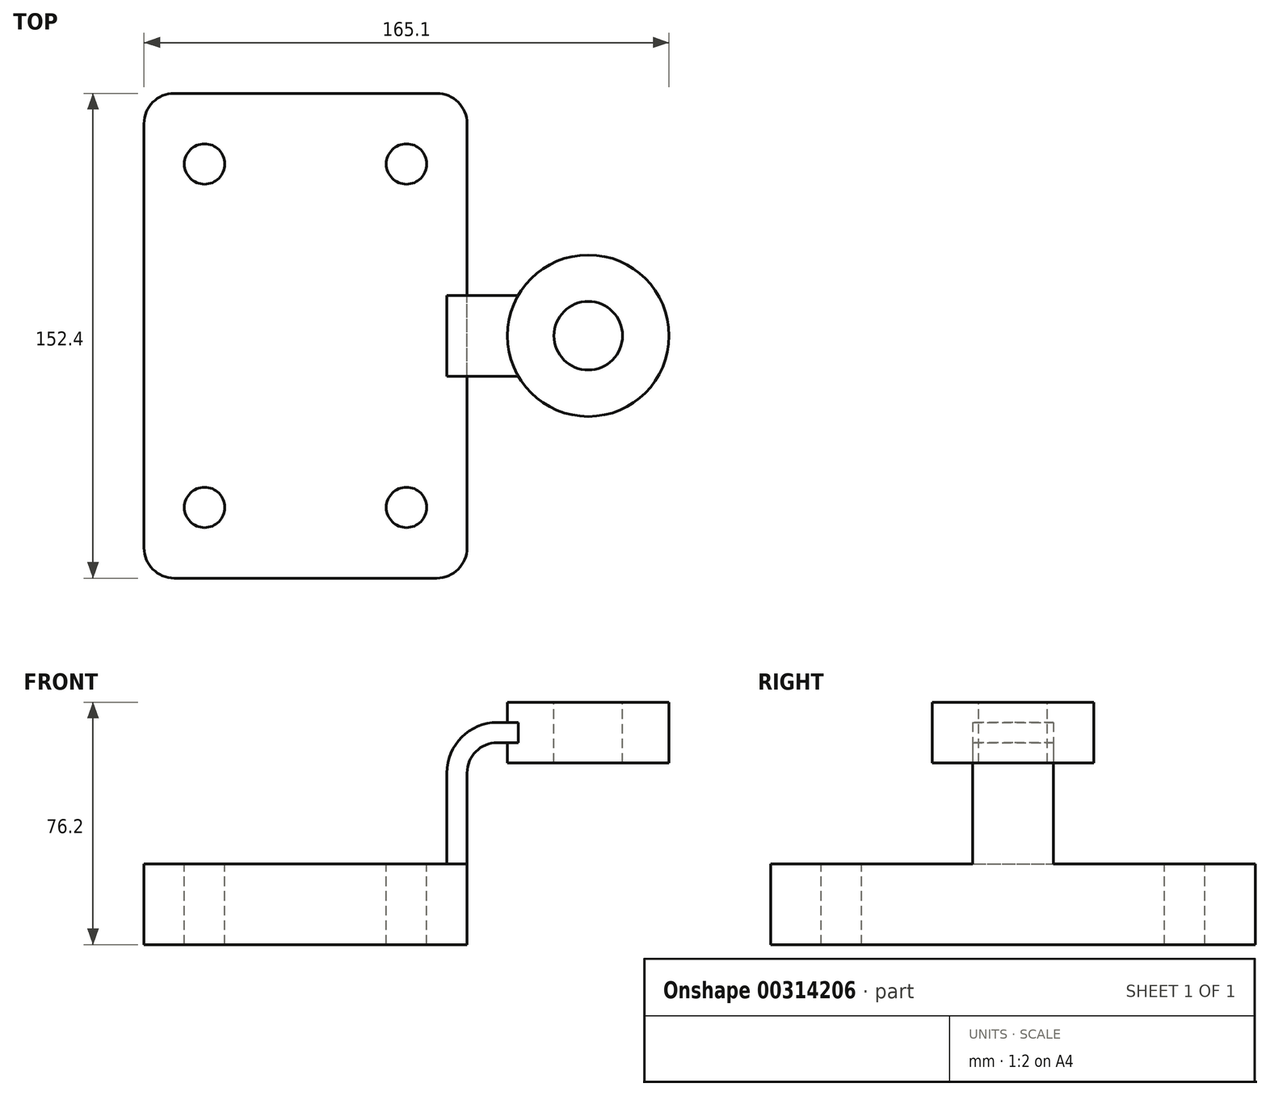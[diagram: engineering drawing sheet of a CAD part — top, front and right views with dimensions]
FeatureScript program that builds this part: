
annotation { "Feature Type Name" : "Feature", "Feature Type Description" : "" }
export const myFeature = defineFeature(function(context is Context, id is Id, definition is map)
    precondition{}
    {
        {
            var Q0;
            Q0=qCreatedBy(makeId("Front.planeOp"),FACE);
            var sketch = newSketch(context, id + "F0", { "sketchPlane" : qUnion([Q0])});
            skLineSegment(sketch, "E0.bottom", {"start": v(-50.8, -12.7) * mm, "end": v(50.8, -12.7) * mm});
            skLineSegment(sketch, "E0.top", {"start": v(-50.8, 12.7) * mm, "end": v(50.8, 12.7) * mm});
            skLineSegment(sketch, "E0.left", {"start": v(-50.8, -12.7) * mm, "end": v(-50.8, 12.7) * mm});
            skLineSegment(sketch, "E0.right", {"start": v(50.8, -12.7) * mm, "end": v(50.8, 12.7) * mm});
            skPoint(sketch, "E0.middle", {"position": v(0, 0) * mm});
            skLineSegment(sketch, "E1.bottom", {"start": v(88.9, 44.45) * mm, "end": v(114.3, 44.45) * mm});
            skLineSegment(sketch, "E1.top", {"start": v(88.9, 63.5) * mm, "end": v(114.3, 63.5) * mm});
            skLineSegment(sketch, "E1.left", {"start": v(88.9, 44.45) * mm, "end": v(88.9, 63.5) * mm});
            skLineSegment(sketch, "E1.right", {"start": v(114.3, 44.45) * mm, "end": v(114.3, 63.5) * mm});
            skPoint(sketch, "E1.middle", {"position": v(101.6, 53.98) * mm});
            skPoint(sketch, "E2.middle", {"position": v(88.9, 63.5) * mm});
            skLineSegment(sketch, "E3", {"start": v(50.8, 12.7) * mm, "end": v(50.8, 41.28) * mm});
            skArc(sketch, "E4", {"start": v(50.8, 41.28) * mm, "mid": v(53.59, 48.01) * mm, "end": v(60.32, 50.8) * mm});
            skLineSegment(sketch, "E5", {"start": v(60.32, 50.8) * mm, "end": v(88.9, 50.8) * mm});
            skLineSegment(sketch, "E6.0", {"start": v(60.32, 57.15) * mm, "end": v(88.9, 57.15) * mm});
            skArc(sketch, "E6.1", {"start": v(44.45, 41.28) * mm, "mid": v(49.1, 52.5) * mm, "end": v(60.32, 57.15) * mm});
            skLineSegment(sketch, "E6.2", {"start": v(44.45, 12.7) * mm, "end": v(44.45, 41.28) * mm});
            skFitSpline(sketch, "E7", {"points": [v(-50.8, 12.7) * mm, v(-2.37, 52.03) * mm, v(60.32, 57.15) * mm], "startDerivative": vector(86.36, 73.43) * mm, "endDerivative": vector(124.87, 0) * mm});
            skLineSegment(sketch, "E8", {"start": v(88.9, 57.15) * mm, "end": v(88.9, 50.8) * mm});
            skSolve(sketch);
        }
        {
            var Q0;
            Q0=makeQuery(id+"F0.imprint","IMPRINT",FACE,{"disambiguationData":[TD([[makeQuery(id+"F0.imprint","IMPRINT",EDGE,{"derivedFrom":sQuery(id+"F0.wireOp",EDGE,"E0.bottom")}),1.0]])]});
            extrude(context, id + "F1", {"entities" : qUnion([Q0]), "endBound" : BoundingType.SYMMETRIC, "depth" : 152.4 * mm});
        }
        {
            var Q0;
            {var subQ0=sQuery(id+"F0.wireOp",EDGE,"E3");Q0=makeQuery(id+"F0.imprint","IMPRINT",FACE,{"disambiguationData":[TD([[makeQuery(id+"F0.imprint","IMPRINT",EDGE,{"derivedFrom":subQ0}),1.0]])]});}
            extrude(context, id + "F2", {"entities" : qUnion([Q0]), "operationType" : NewBodyOperationType.ADD, "endBound" : BoundingType.SYMMETRIC, "depth" : 25.4 * mm});
        }
        {
            var Q0;
            Q0=makeQuery(id+"F0.imprint","IMPRINT",FACE,{"disambiguationData":[TD([[makeQuery(id+"F0.imprint","IMPRINT",EDGE,{"derivedFrom":sQuery(id+"F0.wireOp",EDGE,"E6.1")}),1.0]])]});
            extrude(context, id + "F3", {"entities" : qUnion([Q0]), "operationType" : NewBodyOperationType.ADD, "endBound" : BoundingType.SYMMETRIC, "depth" : 12.7 * mm});
        }
        {
            var Q0;
            {var subQ3=sQuery(id+"F0.wireOp",EDGE,"E1.bottom");Q0=makeQuery(id+"F0.imprint","IMPRINT",FACE,{"disambiguationData":[TD([[makeQuery(id+"F0.imprint","IMPRINT",EDGE,{"derivedFrom":subQ3}),1.0]])]});}
            var Q1;
            Q1=sQuery(id+"F0.wireOp",EDGE,"E1.left");
            revolve(context, id + "F4", {"operationType" : NewBodyOperationType.ADD, "entities" : qUnion([Q0]), "axis" : qUnion([Q1]), "revolveType" : RevolveType.FULL});
        }
        {
            var Q0;
            Q0=makeQuery(id+"F1.opExtrude","CAP_EDGE",EDGE,{"disambiguationData":[OSD([sQuery(id+"F0.wireOp",EDGE,"E0.right")])],"isStart":false});
            var Q1;
            Q1=makeQuery(id+"F1.opExtrude","CAP_EDGE",EDGE,{"disambiguationData":[OSD([sQuery(id+"F0.wireOp",EDGE,"E0.right")])],"isStart":true});
            var Q2;
            Q2=makeQuery(id+"F1.opExtrude","CAP_EDGE",EDGE,{"disambiguationData":[OSD([sQuery(id+"F0.wireOp",EDGE,"E0.left")])],"isStart":true});
            var Q3;
            Q3=makeQuery(id+"F1.opExtrude","CAP_EDGE",EDGE,{"disambiguationData":[OSD([sQuery(id+"F0.wireOp",EDGE,"E0.left")])],"isStart":false});
            fillet(context, id + "F5", {"entities" : qUnion([Q0, Q1, Q2, Q3]), "radius" : 9.52 * mm, "tangentPropagation" : true, "allowEdgeOverflow" : false});
        }
        {
            var Q0;
            Q0=makeQuery(id+"F4.opRevolve","SWEPT_FACE",FACE,{"disambiguationData":[OSD([sQuery(id+"F0.wireOp",EDGE,"E1.top")])]});
            var sketch = newSketch(context, id + "F6", { "sketchPlane" : qUnion([Q0])});
            skCircle(sketch, "E9", {"center": v(88.9, 0) * mm, "radius": 10.78 * mm});
            skSolve(sketch);
        }
        {
            var Q0;
            Q0=makeQuery(id+"F6.imprint","IMPRINT",FACE,{"disambiguationData":[TD([[makeQuery(id+"F6.imprint","IMPRINT",EDGE,{"derivedFrom":sQuery(id+"F6.wireOp",EDGE,"E9")}),1.0]])]});
            var Q1;
            Q1=sQuery(id+"F6.wireOp",EDGE,"E9");
            var Q2;
            Q2=makeQuery(id+"F4.opRevolve","SWEPT_FACE",FACE,{"disambiguationData":[OSD([sQuery(id+"F0.wireOp",EDGE,"E1.bottom")])]});
            var Q3;
            Q3=makeQuery(id+"F4.opRevolve","SWEPT_FACE",FACE,{"disambiguationData":[OSD([sQuery(id+"F0.wireOp",EDGE,"E1.bottom")])]});
            extrude(context, id + "F7", {"entities" : qUnion([Q0]), "operationType" : NewBodyOperationType.REMOVE, "surfaceEntities" : qUnion([Q1]), "endBound" : BoundingType.THROUGH_ALL, "oppositeDirection" : true, "endBoundEntityFace" : qUnion([Q2]), "depth" : 25.4 * mm});
        }
        {
            var Q0;
            Q0=qCreatedBy(makeId("Top.planeOp"),FACE);
            var sketch = newSketch(context, id + "F8", { "sketchPlane" : qUnion([Q0])});
            skCircle(sketch, "E10", {"center": v(31.75, -53.98) * mm, "radius": 6.35 * mm});
            skCircle(sketch, "E11", {"center": v(-31.75, -53.98) * mm, "radius": 6.35 * mm});
            skCircle(sketch, "E12", {"center": v(31.75, 53.98) * mm, "radius": 6.35 * mm});
            skCircle(sketch, "E13", {"center": v(-31.75, 53.98) * mm, "radius": 6.35 * mm});
            skSolve(sketch);
        }
        {
            var Q0;
            Q0=makeQuery(id+"F8.imprint","IMPRINT",FACE,{"disambiguationData":[TD([[makeQuery(id+"F8.imprint","IMPRINT",EDGE,{"derivedFrom":sQuery(id+"F8.wireOp",EDGE,"E11")}),1.0]])]});
            var Q1;
            Q1=makeQuery(id+"F8.imprint","IMPRINT",FACE,{"disambiguationData":[TD([[makeQuery(id+"F8.imprint","IMPRINT",EDGE,{"derivedFrom":sQuery(id+"F8.wireOp",EDGE,"E10")}),1.0]])]});
            var Q2;
            Q2=makeQuery(id+"F8.imprint","IMPRINT",FACE,{"disambiguationData":[TD([[makeQuery(id+"F8.imprint","IMPRINT",EDGE,{"derivedFrom":sQuery(id+"F8.wireOp",EDGE,"E12")}),1.0]])]});
            var Q3;
            Q3=makeQuery(id+"F8.imprint","IMPRINT",FACE,{"disambiguationData":[TD([[makeQuery(id+"F8.imprint","IMPRINT",EDGE,{"derivedFrom":sQuery(id+"F8.wireOp",EDGE,"E13")}),1.0]])]});
            extrude(context, id + "F9", {"entities" : qUnion([Q0, Q1, Q2, Q3]), "operationType" : NewBodyOperationType.REMOVE, "endBound" : BoundingType.SYMMETRIC, "oppositeDirection" : true, "depth" : 25.4 * mm});
        }
    });
